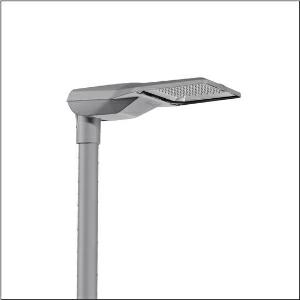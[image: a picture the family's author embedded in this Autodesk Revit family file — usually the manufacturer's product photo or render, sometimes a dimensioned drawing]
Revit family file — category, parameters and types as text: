
# Revit family: streetlight_sl_21_midi___st1_0a_5xe7d33a08nb_63de
name_source: partatom
category: Lighting Fixtures
units: mm (PartAtom-declared; Revit-internal decimal feet)

## family parameters
Cut with Voids When Loaded = No
Host = Face
Light Source = No
Part Type = Normal
Room Calculation Point = No
Round Connector Dimension = Use Diameter
Shared = No

## types (1)
- --- (1 x LED, 22700 lm, 151.2 W, 3000K)
    Apparent Load = 151 VA
    CIE Flux Codes = 40 73 97 100 100
    Color Rendering = 70
    Color Temperature = 3000K
    Default Elevation = 1800 mm
    Description = Streetlight SL 21 midi, mast luminaire, primary light control with lens, of PMMA, primary optical cover: cover, of toughened safety glass, transparent, light distribution: ST1.0a, light emission: direct distribution, primary light characteristic: asymmetric, installation type: post-top, side-entry, LED, 3G 1.5mm², High Power LED, rated luminous flux: 22.700lm, luminous efficacy: 150lm/W, light colour: 730, colour temperature: 3000K, control: flexible luminous flux parameterisation, time-dependent luminous flux control, constant luminous flux control, overheat protection, mains connection: 220..240V, AC, 50/60Hz, connection cable pre-assembled, cable length: 12,5m, wiring characteristics: H07RN-F, start of lifetime: 151W, end of service life: 157W, reduction: 70W, luminaire housing, of diecast aluminium, powder-coated, Siteco® metallic grey (DB 702S), corrosivity category C5 mid according to DIN EN ISO 12944, please order mast flange separately, inclination adjustable: 0°, 5°, 10°, 15°, sealing non-destructively replaceable, multi-level sealing system, length: 644mm, width: 335mm, height: 110mm, mast flange for spigot size: 42mm (side-entry): 5XC10008XM4, 60/48mm (side-entry/post-top): 5XC10108XM2, 76/60mm (side-entry/post-top): 5XC10108XM1, protection rating (complete): IP66, insulation class (complete): insulation class II (safety insulation), certification: CE, ENEC, ENEC+, VDE, impact resistance: IK09, permissible operating ambient temperature for outdoor applications: -40..+50°C, standard-compliant lighting for roads and squares, packaging unit: 1 piece

Light Distribution: ST1.0a
    Height = 111 mm
    Lamp = 1 x LED
    Lamp Light Flux = 22700 lm
    Lamp Power = 151.2 W
    Lamp count = 1
    Length = 644 mm
    Luminous efficacy = 150 lm/W
    Manufacturer = Siteco
    ModVariant = No
    Model = 5XE7D33A08NB
    Number of Poles = 1
    OnlyDefault = Yes
    Power Factor = 1
    Product Name = Streetlight SL 21 midi | ST1.0a
    Product group = mast luminaire | pylon top
    ProductGroupID = 6100
    Protection Class = Protection class II
    Protection Degree = IP 66
    RLX_Detail_Level = 1
    RLX_Emergency_Light_Flux = 0 lm
    RLX_Emergency_Type = 0
    RLX_Emergency_Type_DB = No
    RlxData = <blob elided: 91093 chars, md5=5e5a72d2>
    Socket = socket
    Standby Power = 0 W
    System Light Flux = 22700 lm
    System Power = 151 W
    Type Comments = factory setting: luminous flux: 100 % | Output Level: 100 % | 802 mA
    Type Image = l_1004298.jpg
    URL = http://relux.com
    VarID = @adj_120933
    Voltage = 0 V
    Weight = 0.00 kg
    Width = 336 mm

## geometry (parser evidence)
native form markers: Blend x4, Sweep x10
no freeform markers — native parametric forms only
